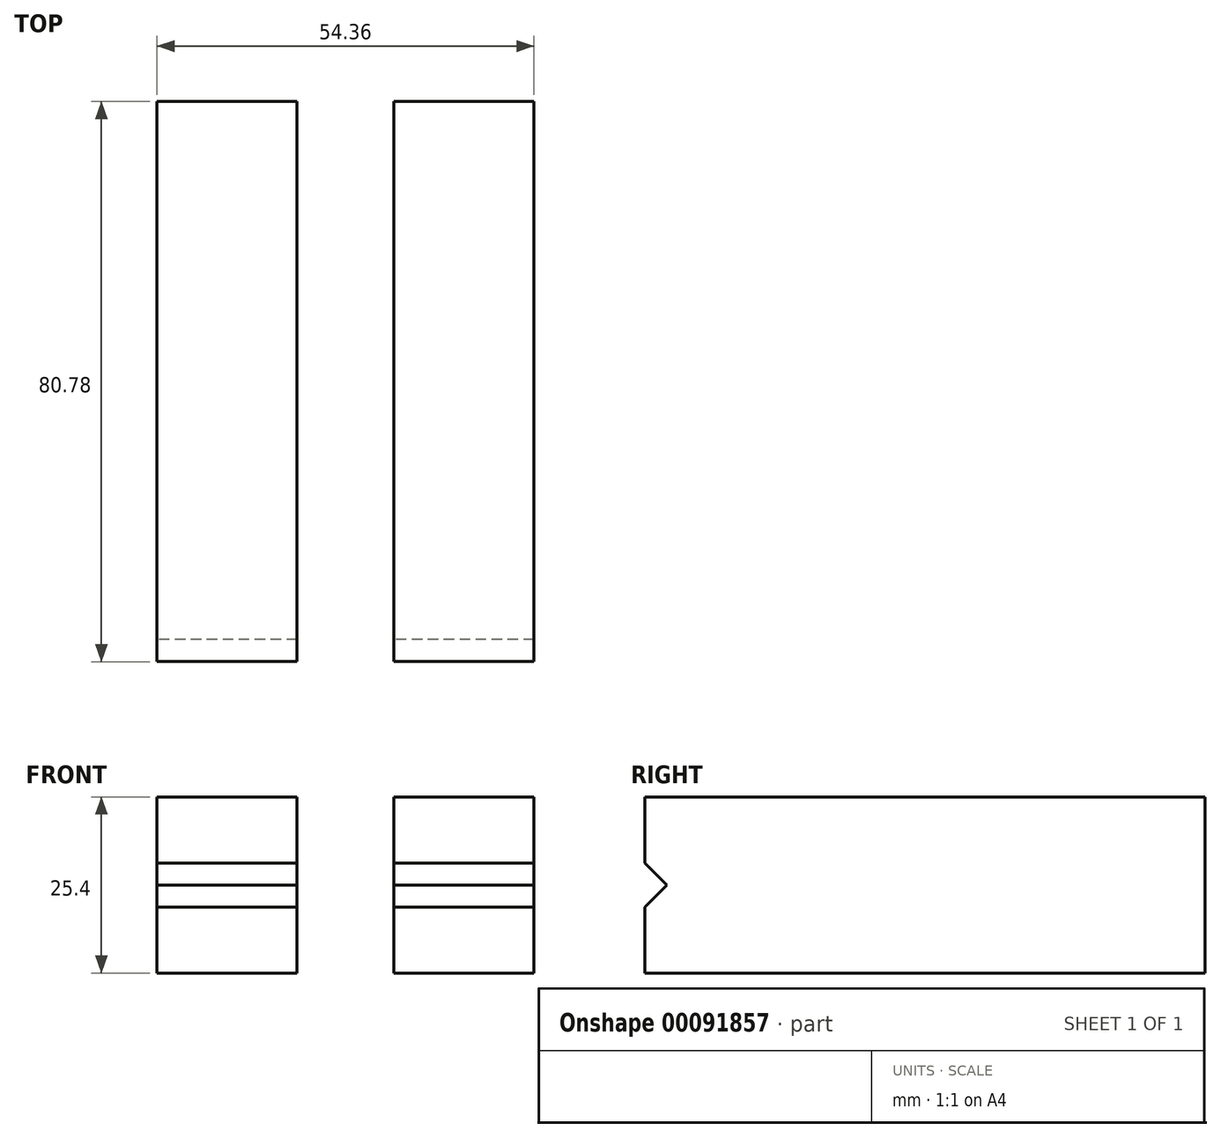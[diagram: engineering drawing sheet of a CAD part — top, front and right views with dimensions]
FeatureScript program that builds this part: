
annotation { "Feature Type Name" : "Feature", "Feature Type Description" : "" }
export const myFeature = defineFeature(function(context is Context, id is Id, definition is map)
    precondition{}
    {
        {
            var Q0;
            Q0=qCreatedBy(makeId("Top.planeOp"),FACE);
            var sketch = newSketch(context, id + "F0", { "sketchPlane" : qUnion([Q0])});
            skLineSegment(sketch, "E0.bottom", {"start": v(27.18, -40.39) * mm, "end": v(-27.18, -40.39) * mm});
            skLineSegment(sketch, "E0.top", {"start": v(27.18, 40.39) * mm, "end": v(-27.18, 40.39) * mm});
            skLineSegment(sketch, "E0.left", {"start": v(27.18, -40.39) * mm, "end": v(27.18, 40.39) * mm});
            skLineSegment(sketch, "E0.right", {"start": v(-27.18, -40.39) * mm, "end": v(-27.18, 40.39) * mm});
            skPoint(sketch, "E0.middle", {"position": v(0, 0) * mm});
            skLineSegment(sketch, "E1.bottom", {"start": v(6.99, -40.39) * mm, "end": v(-6.99, -40.39) * mm});
            skLineSegment(sketch, "E1.top", {"start": v(6.99, 40.39) * mm, "end": v(-6.99, 40.39) * mm});
            skLineSegment(sketch, "E1.left", {"start": v(6.99, -40.39) * mm, "end": v(6.99, 40.39) * mm});
            skLineSegment(sketch, "E1.right", {"start": v(-6.99, -40.39) * mm, "end": v(-6.99, 40.39) * mm});
            skLineSegment(sketch, "E2", {"start": v(-27.18, 16.76) * mm, "end": v(27.18, 16.76) * mm});
            skSolve(sketch);
        }
        {
            var Q0;
            {var subQ0=sQuery(id+"F0.wireOp",EDGE,"E0.right");var subQ1=sQuery(id+"F0.wireOp",EDGE,"E0.bottom");var subQ2=makeQuery(id+"F0.imprint","INTERSECT",VERTEX,{"derivedFrom":[subQ1,subQ0]});Q0=makeQuery(id+"F0.imprint","IMPRINT",FACE,{"disambiguationData":[TD([[makeQuery(id+"F0.imprint","IMPRINT",EDGE,{"disambiguationData":[TD([[subQ2,-1.0]])],"derivedFrom":subQ0}),-1.0]])]});}
            var Q1;
            {var subQ0=sQuery(id+"F0.wireOp",EDGE,"E0.right");var subQ1=sQuery(id+"F0.wireOp",EDGE,"E0.top");var subQ2=makeQuery(id+"F0.imprint","INTERSECT",VERTEX,{"derivedFrom":[subQ1,subQ0]});Q1=makeQuery(id+"F0.imprint","IMPRINT",FACE,{"disambiguationData":[TD([[makeQuery(id+"F0.imprint","IMPRINT",EDGE,{"disambiguationData":[TD([[subQ2,1.0]])],"derivedFrom":subQ0}),-1.0]])]});}
            var Q2;
            {var subQ0=sQuery(id+"F0.wireOp",EDGE,"E1.top");Q2=makeQuery(id+"F0.imprint","IMPRINT",FACE,{"disambiguationData":[TD([[makeQuery(id+"F0.imprint","IMPRINT",EDGE,{"derivedFrom":subQ0}),1.0]])]});}
            var Q3;
            {var subQ0=sQuery(id+"F0.wireOp",EDGE,"E0.left");var subQ1=sQuery(id+"F0.wireOp",EDGE,"E0.top");var subQ2=makeQuery(id+"F0.imprint","INTERSECT",VERTEX,{"derivedFrom":[subQ1,subQ0]});Q3=makeQuery(id+"F0.imprint","IMPRINT",FACE,{"disambiguationData":[TD([[makeQuery(id+"F0.imprint","IMPRINT",EDGE,{"disambiguationData":[TD([[subQ2,1.0]])],"derivedFrom":subQ0}),1.0]])]});}
            var Q4;
            {var subQ0=sQuery(id+"F0.wireOp",EDGE,"E0.left");var subQ1=sQuery(id+"F0.wireOp",EDGE,"E0.bottom");var subQ2=makeQuery(id+"F0.imprint","INTERSECT",VERTEX,{"derivedFrom":[subQ1,subQ0]});Q4=makeQuery(id+"F0.imprint","IMPRINT",FACE,{"disambiguationData":[TD([[makeQuery(id+"F0.imprint","IMPRINT",EDGE,{"disambiguationData":[TD([[subQ2,-1.0]])],"derivedFrom":subQ0}),1.0]])]});}
            extrude(context, id + "F1", {"entities" : qUnion([Q0, Q1, Q2, Q3, Q4]), "depth" : 25.4 * mm});
        }
        {
            var Q0;
            Q0=qCreatedBy(makeId("Right.planeOp"),FACE);
            var sketch = newSketch(context, id + "F2", { "sketchPlane" : qUnion([Q0])});
            skLineSegment(sketch, "E3.0.1", {"start": v(-40.39, 0) * mm, "end": v(-40.39, 25.4) * mm});
            skLineSegment(sketch, "E3.0.3", {"start": v(-40.39, 25.4) * mm, "end": v(-40.39, 0) * mm});
            skPoint(sketch, "E4", {"position": v(-40.39, 12.7) * mm});
            skCircle(sketch, "E5", {"center": v(-40.39, 12.7) * mm, "radius": 3.18 * mm});
            skLineSegment(sketch, "E6", {"start": v(-40.39, 12.7) * mm, "end": v(-37.21, 12.7) * mm});
            skLineSegment(sketch, "E7", {"start": v(-37.21, 12.7) * mm, "end": v(-40.39, 15.88) * mm});
            skLineSegment(sketch, "E8", {"start": v(-37.21, 12.7) * mm, "end": v(-40.39, 9.53) * mm});
            skSolve(sketch);
        }
        {
            var Q0;
            {var subQ0=sQuery(id+"F2.wireOp",EDGE,"E6");Q0=makeQuery(id+"F2.imprint","IMPRINT",FACE,{"disambiguationData":[TD([[makeQuery(id+"F2.imprint","IMPRINT",EDGE,{"derivedFrom":subQ0}),1.0]])]});}
            var Q1;
            {var subQ0=sQuery(id+"F2.wireOp",EDGE,"E6");Q1=makeQuery(id+"F2.imprint","IMPRINT",FACE,{"disambiguationData":[TD([[makeQuery(id+"F2.imprint","IMPRINT",EDGE,{"derivedFrom":subQ0}),-1.0]])]});}
            extrude(context, id + "F3", {"entities" : qUnion([Q0, Q1]), "operationType" : NewBodyOperationType.REMOVE, "endBound" : BoundingType.SYMMETRIC, "depth" : 203.2 * mm});
        }
    });
